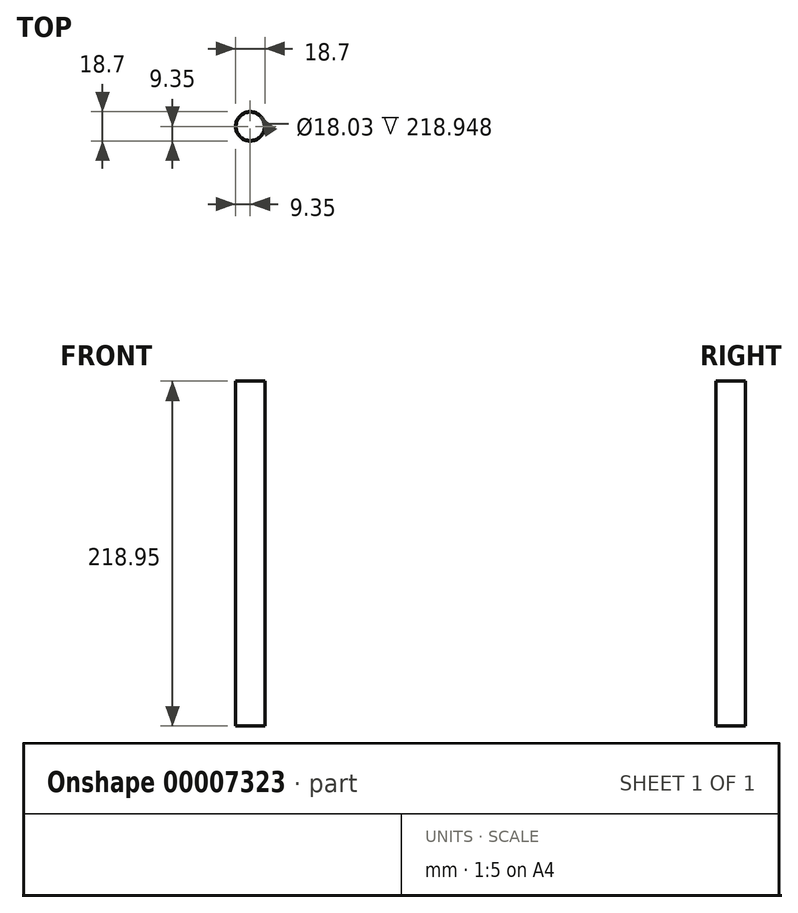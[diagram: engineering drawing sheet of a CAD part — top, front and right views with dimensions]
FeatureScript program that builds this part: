
annotation { "Feature Type Name" : "Feature", "Feature Type Description" : "" }
export const myFeature = defineFeature(function(context is Context, id is Id, definition is map)
    precondition{}
    {
        {
            var Q0;
            Q0=qCreatedBy(makeId("Front.planeOp"),FACE);
            var sketch = newSketch(context, id + "F0", { "sketchPlane" : qUnion([Q0])});
            skLineSegment(sketch, "E0.bottom", {"start": v(9.02, 0) * mm, "end": v(9.35, 0) * mm});
            skLineSegment(sketch, "E0.top", {"start": v(9.02, 218.95) * mm, "end": v(9.35, 218.95) * mm});
            skLineSegment(sketch, "E0.left", {"start": v(9.02, 0) * mm, "end": v(9.02, 218.95) * mm});
            skLineSegment(sketch, "E0.right", {"start": v(9.35, 0) * mm, "end": v(9.35, 218.95) * mm});
            skLineSegment(sketch, "E1", {"start": v(9.02, 0) * mm, "end": v(0, 0) * mm});
            skLineSegment(sketch, "E2", {"start": v(0, 0) * mm, "end": v(0, 218.95) * mm});
            skSolve(sketch);
        }
        {
            var Q0;
            Q0=qSketchRegion(id+"F0",true);
            var Q1;
            Q1=sQuery(id+"F0.wireOp",EDGE,"E2");
            revolve(context, id + "F1", {"entities" : qUnion([Q0]), "axis" : qUnion([Q1]), "revolveType" : RevolveType.FULL});
        }
        {
            var Q0;
            Q0=qCreatedBy(makeId("Top.planeOp"),FACE);
            var sketch = newSketch(context, id + "F2", { "sketchPlane" : qUnion([Q0])});
            skCircle(sketch, "E3", {"center": v(0, 0) * mm, "radius": 63.5 * mm});
            skLineSegment(sketch, "E4", {"start": v(0, 0) * mm, "end": v(0, 63.5) * mm});
            skLineSegment(sketch, "E5", {"start": v(0, 0) * mm, "end": v(55, -31.75) * mm});
            skLineSegment(sketch, "E6.0", {"start": v(0.57, 0) * mm, "end": v(0.57, 63.5) * mm});
            skLineSegment(sketch, "E7.0.MirrorCS", {"start": v(-0.57, 0) * mm, "end": v(-0.57, 63.5) * mm});
            skLineSegment(sketch, "E8.0", {"start": v(-0.28, -0.49) * mm, "end": v(54.7, -32.24) * mm});
            skLineSegment(sketch, "E9", {"start": v(-0.57, 0) * mm, "end": v(0, 0) * mm});
            skLineSegment(sketch, "E10", {"start": v(0, 0) * mm, "end": v(0.57, 0) * mm});
            skLineSegment(sketch, "E11", {"start": v(0, 0) * mm, "end": v(-0.28, -0.49) * mm});
            skLineSegment(sketch, "E12.0.MirrorCS", {"start": v(0.28, 0.49) * mm, "end": v(55.27, -31.26) * mm});
            skLineSegment(sketch, "E13.0.MirrorCS", {"start": v(0, 0) * mm, "end": v(0.28, 0.49) * mm});
            skLineSegment(sketch, "E14.0.MirrorCS", {"start": v(0.28, -0.49) * mm, "end": v(-54.7, -32.24) * mm});
            skLineSegment(sketch, "E14.1.MirrorCS", {"start": v(0, 0) * mm, "end": v(-55, -31.75) * mm});
            skLineSegment(sketch, "E14.2.MirrorCS", {"start": v(-0.28, 0.49) * mm, "end": v(-55.27, -31.26) * mm});
            skLineSegment(sketch, "E15.0.MirrorCS", {"start": v(0, 0) * mm, "end": v(0.28, -0.49) * mm});
            skLineSegment(sketch, "E16.0.MirrorCS", {"start": v(0, 0) * mm, "end": v(-0.28, 0.49) * mm});
            skLineSegment(sketch, "E17.0.MirrorCS", {"start": v(0, 0) * mm, "end": v(0, -63.5) * mm});
            skCircle(sketch, "E18", {"center": v(0, -11.52) * mm, "radius": 2.17 * mm});
            skLineSegment(sketch, "E19", {"start": v(0, 0) * mm, "end": v(-2.17, 0) * mm});
            skLineSegment(sketch, "E20", {"start": v(-2.17, 0) * mm, "end": v(-2.17, -13.7) * mm});
            skLineSegment(sketch, "E21", {"start": v(-2.17, -13.7) * mm, "end": v(0, -13.7) * mm});
            skLineSegment(sketch, "E22.0.MirrorCS", {"start": v(0, 0) * mm, "end": v(2.17, 0) * mm});
            skLineSegment(sketch, "E23.0.MirrorCS", {"start": v(2.17, 0) * mm, "end": v(2.17, -13.7) * mm});
            skLineSegment(sketch, "E24.0.MirrorCS", {"start": v(2.17, -13.7) * mm, "end": v(0, -13.7) * mm});
            skCircle(sketch, "E25.0", {"center": v(0, 0) * mm, "radius": 9.35 * mm});
            skPoint(sketch, "E26", {"position": v(8.1, -4.67) * mm});
            skPoint(sketch, "E27", {"position": v(0, 9.35) * mm});
            skPoint(sketch, "E28", {"position": v(-8.1, -4.67) * mm});
            skPoint(sketch, "E29", {"position": v(0, -9.35) * mm});
            skSolve(sketch);
        }
        {
            var Q0;
            Q0=qCreatedBy(makeId("Top.planeOp"),FACE);
            var sketch = newSketch(context, id + "F3", { "sketchPlane" : qUnion([Q0])});
            skCircle(sketch, "E30.0", {"center": v(0, 0) * mm, "radius": 63.5 * mm});
            skLineSegment(sketch, "E31.0", {"start": v(0.57, 0) * mm, "end": v(0.57, 63.5) * mm});
            skLineSegment(sketch, "E32.0", {"start": v(0, 0) * mm, "end": v(0, 63.5) * mm});
            skLineSegment(sketch, "E33.0", {"start": v(0, 0) * mm, "end": v(0.57, 0) * mm});
            skLineSegment(sketch, "E34.0", {"start": v(-0.57, 0) * mm, "end": v(-0.57, 63.5) * mm});
            skLineSegment(sketch, "E35", {"start": v(0, 0) * mm, "end": v(63.5, 0) * mm});
            skCircle(sketch, "E36", {"center": v(0, 0) * mm, "radius": 0.57 * mm});
            skLineSegment(sketch, "E37.0.MirrorCS", {"start": v(0.57, 0) * mm, "end": v(0.57, -63.5) * mm});
            skLineSegment(sketch, "E38.0.MirrorCS", {"start": v(0, 0) * mm, "end": v(0, -63.5) * mm});
            skLineSegment(sketch, "E39.0.MirrorCS", {"start": v(-0.57, 0) * mm, "end": v(-0.57, -63.5) * mm});
            skLineSegment(sketch, "E40", {"start": v(0, 0.57) * mm, "end": v(63.5, 0.57) * mm});
            skLineSegment(sketch, "E41.0.MirrorCS", {"start": v(0, -0.57) * mm, "end": v(63.5, -0.57) * mm});
            skLineSegment(sketch, "E42.0.MirrorCS", {"start": v(0, 0.57) * mm, "end": v(-63.5, 0.57) * mm});
            skLineSegment(sketch, "E43.0.MirrorCS", {"start": v(0, 0) * mm, "end": v(-63.5, 0) * mm});
            skLineSegment(sketch, "E44.0.MirrorCS", {"start": v(0, -0.57) * mm, "end": v(-63.5, -0.57) * mm});
            skLineSegment(sketch, "E45", {"start": v(0, 0) * mm, "end": v(44.9, 44.9) * mm});
            skCircle(sketch, "E46", {"center": v(8.15, 8.15) * mm, "radius": 2.17 * mm});
            skCircle(sketch, "E47.0", {"center": v(0, 0) * mm, "radius": 9.35 * mm});
            skLineSegment(sketch, "E48", {"start": v(0, 0) * mm, "end": v(-1.54, 1.54) * mm});
            skLineSegment(sketch, "E49", {"start": v(-1.54, 1.54) * mm, "end": v(8.15, 11.22) * mm});
            skLineSegment(sketch, "E50", {"start": v(8.15, 11.22) * mm, "end": v(9.68, 9.68) * mm});
            skLineSegment(sketch, "E51.0.MirrorCS", {"start": v(11.22, 8.15) * mm, "end": v(9.68, 9.68) * mm});
            skLineSegment(sketch, "E52.0.MirrorCS", {"start": v(1.54, -1.54) * mm, "end": v(11.22, 8.15) * mm});
            skLineSegment(sketch, "E53.0.MirrorCS", {"start": v(0, 0) * mm, "end": v(1.54, -1.54) * mm});
            skPoint(sketch, "E54", {"position": v(9.35, 0) * mm});
            skPoint(sketch, "E55", {"position": v(-9.35, 0) * mm});
            skPoint(sketch, "E56", {"position": v(0, 9.35) * mm});
            skPoint(sketch, "E57", {"position": v(0, -9.35) * mm});
            skPoint(sketch, "E58", {"position": v(6.6, 6.6) * mm});
            skSolve(sketch);
        }
        {
            var Q0;
            Q0=qCreatedBy(makeId("Top.planeOp"),FACE);
            var sketch = newSketch(context, id + "F4", { "sketchPlane" : qUnion([Q0])});
            skCircle(sketch, "E59.0", {"center": v(0, 0) * mm, "radius": 63.5 * mm});
            skCircle(sketch, "E60.0", {"center": v(0, 0) * mm, "radius": 9.35 * mm});
            skLineSegment(sketch, "E61.0", {"start": v(0.57, 0) * mm, "end": v(0.57, 63.5) * mm});
            skLineSegment(sketch, "E62.0", {"start": v(0, 0) * mm, "end": v(0, 63.5) * mm});
            skLineSegment(sketch, "E63.0", {"start": v(-0.57, 0) * mm, "end": v(-0.57, 63.5) * mm});
            skLineSegment(sketch, "E64.0", {"start": v(0, 0) * mm, "end": v(0.57, 0) * mm});
            skLineSegment(sketch, "E65.0", {"start": v(0, 0) * mm, "end": v(0, -63.5) * mm});
            skLineSegment(sketch, "E66.0", {"start": v(2.17, 0) * mm, "end": v(2.17, -13.7) * mm});
            skLineSegment(sketch, "E67.0", {"start": v(-2.17, 0) * mm, "end": v(-2.17, -13.7) * mm});
            skLineSegment(sketch, "E68.0", {"start": v(0, 0) * mm, "end": v(-2.17, 0) * mm});
            skLineSegment(sketch, "E69.0", {"start": v(0, 0) * mm, "end": v(2.17, 0) * mm});
            skCircle(sketch, "E70.0", {"center": v(0, -11.52) * mm, "radius": 2.17 * mm});
            skLineSegment(sketch, "E71.0", {"start": v(-2.17, -13.7) * mm, "end": v(0, -13.7) * mm});
            skLineSegment(sketch, "E72.0", {"start": v(2.17, -13.7) * mm, "end": v(0, -13.7) * mm});
            skLineSegment(sketch, "E73", {"start": v(0, 0) * mm, "end": v(60.4, 19.62) * mm});
            skCircle(sketch, "E74", {"center": v(0, 0) * mm, "radius": 0.57 * mm});
            skLineSegment(sketch, "E75", {"start": v(0, 0) * mm, "end": v(37.32, -51.37) * mm});
            skLineSegment(sketch, "E76", {"start": v(-0.17, 0.54) * mm, "end": v(60.22, 20.16) * mm});
            skLineSegment(sketch, "E77", {"start": v(0, 0) * mm, "end": v(-0.17, 0.54) * mm});
            skLineSegment(sketch, "E78.0.MirrorCS", {"start": v(0.17, -0.54) * mm, "end": v(60.56, 19.08) * mm});
            skLineSegment(sketch, "E79.0.MirrorCS", {"start": v(0, 0) * mm, "end": v(0.17, -0.54) * mm});
            skLineSegment(sketch, "E80", {"start": v(0.46, 0.33) * mm, "end": v(37.78, -51.04) * mm});
            skLineSegment(sketch, "E81", {"start": v(0, 0) * mm, "end": v(0.46, 0.33) * mm});
            skLineSegment(sketch, "E82.0.MirrorCS", {"start": v(-0.46, -0.33) * mm, "end": v(36.87, -51.7) * mm});
            skLineSegment(sketch, "E83.0.MirrorCS", {"start": v(0, 0) * mm, "end": v(-0.46, -0.33) * mm});
            skLineSegment(sketch, "E84.0.MirrorCS", {"start": v(0.17, 0.54) * mm, "end": v(-60.22, 20.16) * mm});
            skLineSegment(sketch, "E85.0.MirrorCS", {"start": v(0, 0) * mm, "end": v(-60.4, 19.62) * mm});
            skLineSegment(sketch, "E86.0.MirrorCS", {"start": v(-0.17, -0.54) * mm, "end": v(-60.56, 19.08) * mm});
            skLineSegment(sketch, "E87.0.MirrorCS", {"start": v(0, 0) * mm, "end": v(0.17, 0.54) * mm});
            skLineSegment(sketch, "E88.0.MirrorCS", {"start": v(0, 0) * mm, "end": v(-0.17, -0.54) * mm});
            skLineSegment(sketch, "E89.0.MirrorCS", {"start": v(-0.46, 0.33) * mm, "end": v(-37.78, -51.04) * mm});
            skLineSegment(sketch, "E90.0.MirrorCS", {"start": v(0, 0) * mm, "end": v(-37.32, -51.37) * mm});
            skLineSegment(sketch, "E91.0.MirrorCS", {"start": v(0.46, -0.33) * mm, "end": v(-36.87, -51.7) * mm});
            skLineSegment(sketch, "E92.0.MirrorCS", {"start": v(0, 0) * mm, "end": v(0.46, -0.33) * mm});
            skLineSegment(sketch, "E93.0.MirrorCS", {"start": v(0, 0) * mm, "end": v(-0.46, 0.33) * mm});
            skPoint(sketch, "E94", {"position": v(0, 9.35) * mm});
            skPoint(sketch, "E95", {"position": v(8.89, 2.89) * mm});
            skPoint(sketch, "E96", {"position": v(5.5, -7.56) * mm});
            skPoint(sketch, "E97", {"position": v(-5.5, -7.56) * mm});
            skPoint(sketch, "E98", {"position": v(-8.89, 2.89) * mm});
            skSolve(sketch);
        }
        {
            var Q0;
            Q0=sQuery(id+"F2.wireOp",EDGE,"E5");
            var Q1;
            Q1=sQuery(id+"F2.wireOp",VERTEX,"E26");
            cPlane(context, id + "F5", {"entities" : qUnion([Q0, Q1]), "cplaneType" : CPlaneType.LINE_POINT, "offset" : 152.4 * mm, "width" : 152.4 * mm, "height" : 152.4 * mm});
        }
        {
            var Q0;
            Q0=sQuery(id+"F2.wireOp",EDGE,"E14.1.MirrorCS");
            var Q1;
            Q1=sQuery(id+"F2.wireOp",VERTEX,"E28");
            cPlane(context, id + "F6", {"entities" : qUnion([Q0, Q1]), "cplaneType" : CPlaneType.LINE_POINT, "offset" : 152.4 * mm, "width" : 152.4 * mm, "height" : 152.4 * mm});
        }
        {
            var Q0;
            Q0=sQuery(id+"F2.wireOp",EDGE,"E4");
            var Q1;
            Q1=sQuery(id+"F2.wireOp",VERTEX,"E27");
            cPlane(context, id + "F7", {"entities" : qUnion([Q0, Q1]), "cplaneType" : CPlaneType.LINE_POINT, "offset" : 152.4 * mm, "width" : 152.4 * mm, "height" : 152.4 * mm});
        }
        {
            var Q0;
            Q0=sQuery(id+"F2.wireOp",EDGE,"E17.0.MirrorCS");
            var Q1;
            Q1=sQuery(id+"F2.wireOp",VERTEX,"E29");
            cPlane(context, id + "F8", {"entities" : qUnion([Q0, Q1]), "cplaneType" : CPlaneType.LINE_POINT, "offset" : 152.4 * mm, "width" : 152.4 * mm, "height" : 152.4 * mm});
        }
        {
            var Q0;
            Q0=sQuery(id+"F3.wireOp",EDGE,"E45");
            var Q1;
            Q1=sQuery(id+"F3.wireOp",VERTEX,"E58");
            cPlane(context, id + "F9", {"entities" : qUnion([Q0, Q1]), "cplaneType" : CPlaneType.LINE_POINT, "offset" : 152.4 * mm, "width" : 152.4 * mm, "height" : 152.4 * mm});
        }
        {
            var Q0;
            Q0=sQuery(id+"F4.wireOp",EDGE,"E73");
            var Q1;
            Q1=sQuery(id+"F4.wireOp",VERTEX,"E95");
            cPlane(context, id + "F10", {"entities" : qUnion([Q0, Q1]), "cplaneType" : CPlaneType.LINE_POINT, "offset" : 152.4 * mm, "width" : 152.4 * mm, "height" : 152.4 * mm});
        }
        {
            var Q0;
            Q0=sQuery(id+"F4.wireOp",EDGE,"E75");
            var Q1;
            Q1=sQuery(id+"F4.wireOp",VERTEX,"E96");
            cPlane(context, id + "F11", {"entities" : qUnion([Q0, Q1]), "cplaneType" : CPlaneType.LINE_POINT, "offset" : 152.4 * mm, "width" : 152.4 * mm, "height" : 152.4 * mm});
        }
        {
            var Q0;
            Q0=sQuery(id+"F4.wireOp",EDGE,"E90.0.MirrorCS");
            var Q1;
            Q1=sQuery(id+"F4.wireOp",VERTEX,"E97");
            cPlane(context, id + "F12", {"entities" : qUnion([Q0, Q1]), "cplaneType" : CPlaneType.LINE_POINT, "offset" : 152.4 * mm, "width" : 152.4 * mm, "height" : 152.4 * mm});
        }
        {
            var Q0;
            Q0=sQuery(id+"F4.wireOp",EDGE,"E85.0.MirrorCS");
            var Q1;
            Q1=sQuery(id+"F4.wireOp",VERTEX,"E98");
            cPlane(context, id + "F13", {"entities" : qUnion([Q0, Q1]), "cplaneType" : CPlaneType.LINE_POINT, "offset" : 152.4 * mm, "width" : 152.4 * mm, "height" : 152.4 * mm});
        }
        {
            var Q0;
            Q0=qCreatedBy(makeId("Top.planeOp"),FACE);
            var sketch = newSketch(context, id + "F14", { "sketchPlane" : qUnion([Q0])});
            skLineSegment(sketch, "E99.0", {"start": v(0, 0) * mm, "end": v(-55, -31.75) * mm});
            skCircle(sketch, "E100.0", {"center": v(0, 0) * mm, "radius": 9.35 * mm});
            skCircle(sketch, "E100.1", {"center": v(0, 0) * mm, "radius": 63.5 * mm});
            skLineSegment(sketch, "E101", {"start": v(0, 0) * mm, "end": v(0.4, -0.69) * mm});
            skLineSegment(sketch, "E102", {"start": v(0.4, -0.69) * mm, "end": v(-54.6, -32.43) * mm});
            skCircle(sketch, "E103", {"center": v(-8.16, -8.13) * mm, "radius": 2.17 * mm});
            skLineSegment(sketch, "E104", {"start": v(0, 0) * mm, "end": v(-8.16, -8.13) * mm});
            skSolve(sketch);
        }
        {
            var Q0;
            Q0=sQuery(id+"F14.wireOp",VERTEX,"E99.0.start");
            var Q1;
            Q1=sQuery(id+"F0.wireOp",VERTEX,"E2.end");
            var Q2;
            Q2=sQuery(id+"F14.wireOp",VERTEX,"E103.center");
            cPlane(context, id + "F15", {"entities" : qUnion([Q0, Q1, Q2]), "cplaneType" : CPlaneType.THREE_POINT, "offset" : 152.4 * mm, "width" : 152.4 * mm, "height" : 152.4 * mm});
        }
        {
            var Q0;
            Q0=qCreatedBy(id+"F15.planeOp",FACE);
            var sketch = newSketch(context, id + "F16", { "sketchPlane" : qUnion([Q0])});
            skLineSegment(sketch, "E105.0", {"start": v(0, 0) * mm, "end": v(0, 218.95) * mm});
            skLineSegment(sketch, "E106.1", {"start": v(0, 0) * mm, "end": v(11.52, 0) * mm});
            skLineSegment(sketch, "E107", {"start": v(11.52, 0) * mm, "end": v(11.52, 218.95) * mm});
            skLineSegment(sketch, "E108", {"start": v(11.52, 218.95) * mm, "end": v(0, 218.95) * mm});
            skSolve(sketch);
        }
    });
